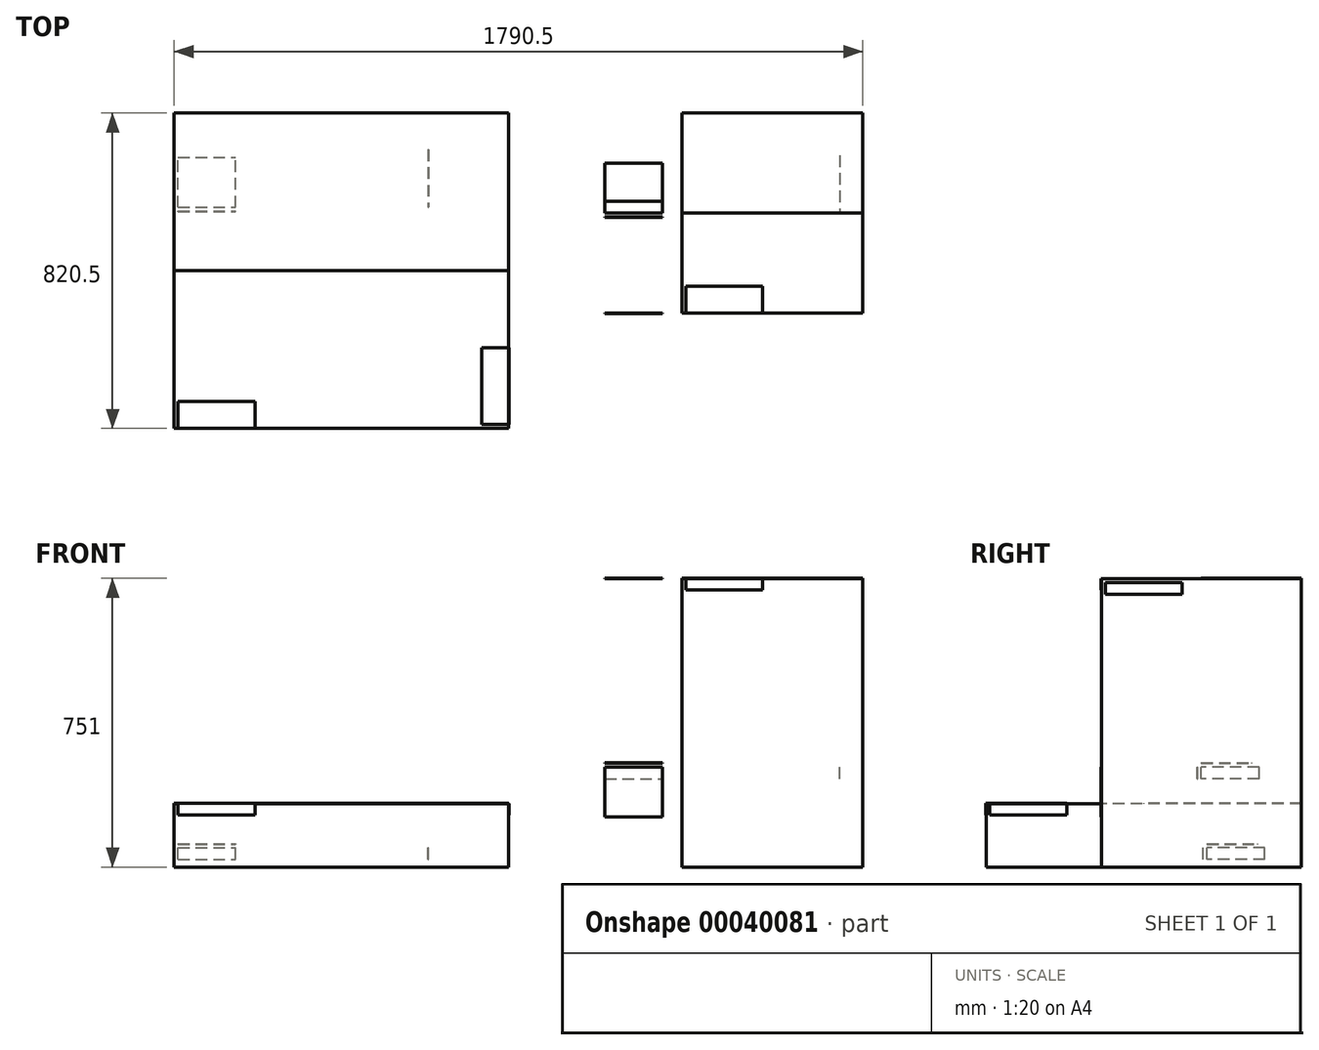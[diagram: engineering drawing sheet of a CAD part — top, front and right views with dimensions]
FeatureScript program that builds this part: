
annotation { "Feature Type Name" : "Feature", "Feature Type Description" : "" }
export const myFeature = defineFeature(function(context is Context, id is Id, definition is map)
    precondition{}
    {
        {
            var Q0;
            Q0=qCreatedBy(makeId("Top.planeOp"),FACE);
            var sketch = newSketch(context, id + "F0", { "sketchPlane" : qUnion([Q0])});
            skLineSegment(sketch, "E0.bottom", {"start": v(-224.33, 780.37) * mm, "end": v(645.67, 780.37) * mm});
            skLineSegment(sketch, "E0.top", {"start": v(-224.33, -39.63) * mm, "end": v(645.67, -39.63) * mm});
            skLineSegment(sketch, "E0.left", {"start": v(-224.33, 780.37) * mm, "end": v(-224.33, -39.63) * mm});
            skLineSegment(sketch, "E0.right", {"start": v(645.67, 780.37) * mm, "end": v(645.67, -39.63) * mm});
            skLineSegment(sketch, "E1.bottom", {"start": v(1095.67, 260.37) * mm, "end": v(1565.67, 260.37) * mm});
            skLineSegment(sketch, "E1.top", {"start": v(1095.67, 780.37) * mm, "end": v(1565.67, 780.37) * mm});
            skLineSegment(sketch, "E1.left", {"start": v(1095.67, 260.37) * mm, "end": v(1095.67, 780.37) * mm});
            skLineSegment(sketch, "E1.right", {"start": v(1565.67, 260.37) * mm, "end": v(1565.67, 780.37) * mm});
            skLineSegment(sketch, "E2.bottom", {"start": v(-224.33, 980.37) * mm, "end": v(-74.33, 980.37) * mm});
            skLineSegment(sketch, "E2.top", {"start": v(-224.33, 1110.37) * mm, "end": v(-74.33, 1110.37) * mm});
            skLineSegment(sketch, "E2.left", {"start": v(-224.33, 980.37) * mm, "end": v(-224.33, 1110.37) * mm});
            skLineSegment(sketch, "E2.right", {"start": v(-74.33, 980.37) * mm, "end": v(-74.33, 1110.37) * mm});
            skLineSegment(sketch, "E3.bottom", {"start": v(-224.33, 880.37) * mm, "end": v(-74.33, 880.37) * mm});
            skLineSegment(sketch, "E3.top", {"start": v(-224.33, 910.37) * mm, "end": v(-74.33, 910.37) * mm});
            skLineSegment(sketch, "E3.left", {"start": v(-224.33, 880.37) * mm, "end": v(-224.33, 910.37) * mm});
            skLineSegment(sketch, "E3.right", {"start": v(-74.33, 880.37) * mm, "end": v(-74.33, 910.37) * mm});
            skSolve(sketch);
        }
        {
            var Q0;
            Q0=makeQuery(id+"F0.imprint","IMPRINT",FACE,{"disambiguationData":[TD([[makeQuery(id+"F0.imprint","IMPRINT",EDGE,{"derivedFrom":sQuery(id+"F0.wireOp",EDGE,"E0.bottom")}),-1.0]])]});
            extrude(context, id + "F1", {"entities" : qUnion([Q0]), "offsetDistance" : 25 * mm, "depth" : 165 * mm});
        }
        {
            var Q0;
            Q0=makeQuery(id+"F0.imprint","IMPRINT",FACE,{"disambiguationData":[TD([[makeQuery(id+"F0.imprint","IMPRINT",EDGE,{"derivedFrom":sQuery(id+"F0.wireOp",EDGE,"E1.bottom")}),1.0]])]});
            extrude(context, id + "F2", {"entities" : qUnion([Q0]), "operationType" : NewBodyOperationType.ADD, "offsetDistance" : 25 * mm, "depth" : 750 * mm});
        }
        {
            var Q0;
            Q0=makeQuery(id+"F0.imprint","IMPRINT",FACE,{"disambiguationData":[TD([[makeQuery(id+"F0.imprint","IMPRINT",EDGE,{"derivedFrom":sQuery(id+"F0.wireOp",EDGE,"E2.bottom")}),1.0]])]});
            var Q1;
            Q1=makeQuery(id+"F0.imprint","IMPRINT",FACE,{"disambiguationData":[TD([[makeQuery(id+"F0.imprint","IMPRINT",EDGE,{"derivedFrom":sQuery(id+"F0.wireOp",EDGE,"E3.bottom")}),1.0]])]});
            extrude(context, id + "F3", {"entities" : qUnion([Q0, Q1]), "depth" : 1 * mm});
        }
        {
            var Q0;
            Q0=makeQuery(id+"F3.opExtrude","SWEPT_BODY",BODY,{"disambiguationData":[OSD([sQuery(id+"F0.wireOp",EDGE,"E2.bottom"),sQuery(id+"F0.wireOp",EDGE,"E2.top"),sQuery(id+"F0.wireOp",EDGE,"E2.left"),sQuery(id+"F0.wireOp",EDGE,"E2.right")])]});
            transform(context, id + "F4", {"entities" : qUnion([Q0]), "transformType" : TransformType.TRANSLATION_3D, "dx" : 10 * mm, "dy" : -445 * mm, "dz" : 60 * mm, "makeCopy" : false});
        }
        {
            var Q0;
            Q0=makeQuery(id+"F3.opExtrude","SWEPT_BODY",BODY,{"disambiguationData":[OSD([sQuery(id+"F0.wireOp",EDGE,"E2.bottom"),sQuery(id+"F0.wireOp",EDGE,"E2.top"),sQuery(id+"F0.wireOp",EDGE,"E2.left"),sQuery(id+"F0.wireOp",EDGE,"E2.right")])]});
            transform(context, id + "F5", {"entities" : qUnion([Q0]), "transformType" : TransformType.TRANSLATION_3D, "dx" : 1110 * mm, "dy" : -15 * mm, "dz" : 210 * mm, "makeCopy" : true});
        }
        {
            var Q0;
            Q0=makeQuery(id+"F3.opExtrude","SWEPT_BODY",BODY,{"disambiguationData":[OSD([sQuery(id+"F0.wireOp",EDGE,"E3.bottom"),sQuery(id+"F0.wireOp",EDGE,"E3.top"),sQuery(id+"F0.wireOp",EDGE,"E3.left"),sQuery(id+"F0.wireOp",EDGE,"E3.right")])]});
            var Q1;
            Q1=makeQuery(id+"F3.opExtrude","CAP_EDGE",EDGE,{"disambiguationData":[OSD([sQuery(id+"F0.wireOp",EDGE,"E3.bottom")])],"isStart":true});
            transform(context, id + "F6", {"entities" : qUnion([Q0]), "transformType" : TransformType.ROTATION, "transformAxis" : qUnion([Q1]), "angle" : 90 * degree, "makeCopy" : false});
        }
        {
            var Q0;
            Q0=makeQuery(id+"F3.opExtrude","SWEPT_BODY",BODY,{"disambiguationData":[OSD([sQuery(id+"F0.wireOp",EDGE,"E3.bottom"),sQuery(id+"F0.wireOp",EDGE,"E3.top"),sQuery(id+"F0.wireOp",EDGE,"E3.left"),sQuery(id+"F0.wireOp",EDGE,"E3.right")])]});
            transform(context, id + "F7", {"entities" : qUnion([Q0]), "transformType" : TransformType.TRANSLATION_3D, "dx" : 10 * mm, "dy" : -355 * mm, "dz" : 20 * mm, "makeCopy" : false});
        }
        {
            var Q0;
            Q0=makeQuery(id+"F3.opExtrude","SWEPT_BODY",BODY,{"disambiguationData":[OSD([sQuery(id+"F0.wireOp",EDGE,"E3.bottom"),sQuery(id+"F0.wireOp",EDGE,"E3.top"),sQuery(id+"F0.wireOp",EDGE,"E3.left"),sQuery(id+"F0.wireOp",EDGE,"E3.right")])]});
            transform(context, id + "F8", {"entities" : qUnion([Q0]), "transformType" : TransformType.TRANSLATION_3D, "dx" : 1110 * mm, "dy" : -15 * mm, "dz" : 210 * mm, "makeCopy" : true});
        }
        {
            var Q0;
            Q0=makeQuery(id+"F3.opExtrude","SWEPT_BODY",BODY,{"disambiguationData":[OSD([sQuery(id+"F0.wireOp",EDGE,"E3.bottom"),sQuery(id+"F0.wireOp",EDGE,"E3.top"),sQuery(id+"F0.wireOp",EDGE,"E3.left"),sQuery(id+"F0.wireOp",EDGE,"E3.right")])]});
            var Q1;
            Q1=makeQuery(id+"F3.opExtrude","CAP_EDGE",EDGE,{"disambiguationData":[OSD([sQuery(id+"F0.wireOp",EDGE,"E3.right")])],"isStart":true});
            transform(context, id + "F9", {"entities" : qUnion([Q0]), "transformType" : TransformType.ROTATION, "transformAxis" : qUnion([Q1]), "angle" : 270 * degree, "makeCopy" : true});
        }
        {
            var Q0;
            Q0=makeQuery(id+"F9.opPattern","COPY",BODY,{"derivedFrom":makeQuery(id+"F3.opExtrude","SWEPT_BODY",BODY,{"disambiguationData":[OSD([sQuery(id+"F0.wireOp",EDGE,"E3.bottom"),sQuery(id+"F0.wireOp",EDGE,"E3.top"),sQuery(id+"F0.wireOp",EDGE,"E3.left"),sQuery(id+"F0.wireOp",EDGE,"E3.right")])]}),"instanceName":"1"});
            transform(context, id + "F10", {"entities" : qUnion([Q0]), "transformType" : TransformType.TRANSLATION_3D, "dx" : 501 * mm, "dy" : 10 * mm, "dz" : 0 * mm, "makeCopy" : false});
        }
        {
            var Q0;
            Q0=makeQuery(id+"F8.opPattern","COPY",BODY,{"derivedFrom":makeQuery(id+"F3.opExtrude","SWEPT_BODY",BODY,{"disambiguationData":[OSD([sQuery(id+"F0.wireOp",EDGE,"E3.bottom"),sQuery(id+"F0.wireOp",EDGE,"E3.top"),sQuery(id+"F0.wireOp",EDGE,"E3.left"),sQuery(id+"F0.wireOp",EDGE,"E3.right")])]}),"instanceName":"1"});
            var Q1;
            Q1=makeQuery(id+"F8.opPattern","COPY",EDGE,{"derivedFrom":makeQuery(id+"F3.opExtrude","CAP_EDGE",EDGE,{"disambiguationData":[OSD([sQuery(id+"F0.wireOp",EDGE,"E3.right")])],"isStart":true}),"instanceName":"1"});
            transform(context, id + "F11", {"entities" : qUnion([Q0]), "transformType" : TransformType.ROTATION, "transformAxis" : qUnion([Q1]), "angle" : 270 * degree, "makeCopy" : true});
        }
        {
            var Q0;
            Q0=makeQuery(id+"F11.opPattern","COPY",BODY,{"derivedFrom":makeQuery(id+"F8.opPattern","COPY",BODY,{"derivedFrom":makeQuery(id+"F3.opExtrude","SWEPT_BODY",BODY,{"disambiguationData":[OSD([sQuery(id+"F0.wireOp",EDGE,"E3.bottom"),sQuery(id+"F0.wireOp",EDGE,"E3.top"),sQuery(id+"F0.wireOp",EDGE,"E3.left"),sQuery(id+"F0.wireOp",EDGE,"E3.right")])]}),"instanceName":"1"}),"instanceName":"1"});
            transform(context, id + "F12", {"entities" : qUnion([Q0]), "transformType" : TransformType.TRANSLATION_3D, "dx" : 461 * mm, "dy" : 10 * mm, "dz" : 0 * mm, "makeCopy" : false});
        }
        {
            var Q0;
            Q0=makeQuery(id+"F2.opExtrude","CAP_FACE",FACE,{"disambiguationData":[OSD([sQuery(id+"F0.wireOp",EDGE,"E1.bottom"),sQuery(id+"F0.wireOp",EDGE,"E1.top"),sQuery(id+"F0.wireOp",EDGE,"E1.left"),sQuery(id+"F0.wireOp",EDGE,"E1.right")])],"isStart":false});
            var sketch = newSketch(context, id + "F13", { "sketchPlane" : qUnion([Q0])});
            skLineSegment(sketch, "E4.bottom", {"start": v(1095.67, 780.37) * mm, "end": v(1565.67, 780.37) * mm});
            skLineSegment(sketch, "E4.top", {"start": v(1095.67, 520.37) * mm, "end": v(1565.67, 520.37) * mm});
            skLineSegment(sketch, "E4.left", {"start": v(1095.67, 780.37) * mm, "end": v(1095.67, 520.37) * mm});
            skLineSegment(sketch, "E4.right", {"start": v(1565.67, 780.37) * mm, "end": v(1565.67, 520.37) * mm});
            skLineSegment(sketch, "E5.bottom", {"start": v(895.67, 520.37) * mm, "end": v(1045.67, 520.37) * mm});
            skLineSegment(sketch, "E5.top", {"start": v(895.67, 550.37) * mm, "end": v(1045.67, 550.37) * mm});
            skLineSegment(sketch, "E5.left", {"start": v(895.67, 520.37) * mm, "end": v(895.67, 550.37) * mm});
            skLineSegment(sketch, "E5.right", {"start": v(1045.67, 520.37) * mm, "end": v(1045.67, 550.37) * mm});
            skSolve(sketch);
        }
        {
            var Q0;
            Q0 = qSketchRegion(id + "F13", true);
            extrude(context, id + "F14", {"entities" : qUnion([Q0]), "depth" : 1 * mm});
        }
        {
            var Q0;
            Q0=makeQuery(id+"F2.opExtrude","SWEPT_FACE",FACE,{"disambiguationData":[OSD([sQuery(id+"F0.wireOp",EDGE,"E1.bottom")])]});
            var sketch = newSketch(context, id + "F15", { "sketchPlane" : qUnion([Q0])});
            skLineSegment(sketch, "E6.bottom", {"start": v(895.67, 260) * mm, "end": v(1045.67, 260) * mm});
            skLineSegment(sketch, "E6.top", {"start": v(895.67, 130) * mm, "end": v(1045.67, 130) * mm});
            skLineSegment(sketch, "E6.left", {"start": v(895.67, 260) * mm, "end": v(895.67, 130) * mm});
            skLineSegment(sketch, "E6.right", {"start": v(1045.67, 260) * mm, "end": v(1045.67, 130) * mm});
            skSolve(sketch);
        }
        {
            var Q0;
            Q0=makeQuery(id+"F15.imprint","IMPRINT",FACE,{"disambiguationData":[TD([[makeQuery(id+"F15.imprint","IMPRINT",EDGE,{"derivedFrom":sQuery(id+"F15.wireOp",EDGE,"E6.bottom")}),-1.0]])]});
            extrude(context, id + "F16", {"entities" : qUnion([Q0]), "depth" : 1 * mm});
        }
        {
            var Q0;
            Q0=makeQuery(id+"F1.opExtrude","CAP_FACE",FACE,{"disambiguationData":[OSD([sQuery(id+"F0.wireOp",EDGE,"E0.bottom"),sQuery(id+"F0.wireOp",EDGE,"E0.top"),sQuery(id+"F0.wireOp",EDGE,"E0.left"),sQuery(id+"F0.wireOp",EDGE,"E0.right")])],"isStart":false});
            var sketch = newSketch(context, id + "F17", { "sketchPlane" : qUnion([Q0])});
            skLineSegment(sketch, "E7.bottom", {"start": v(-214.33, -39.63) * mm, "end": v(-14.33, -39.63) * mm});
            skLineSegment(sketch, "E7.top", {"start": v(-214.33, 30.37) * mm, "end": v(-14.33, 30.37) * mm});
            skLineSegment(sketch, "E7.left", {"start": v(-214.33, -39.63) * mm, "end": v(-214.33, 30.37) * mm});
            skLineSegment(sketch, "E7.right", {"start": v(-14.33, -39.63) * mm, "end": v(-14.33, 30.37) * mm});
            skLineSegment(sketch, "E8.bottom", {"start": v(575.67, 170.37) * mm, "end": v(645.67, 170.37) * mm});
            skLineSegment(sketch, "E8.top", {"start": v(575.67, -29.63) * mm, "end": v(645.67, -29.63) * mm});
            skLineSegment(sketch, "E8.left", {"start": v(575.67, 170.37) * mm, "end": v(575.67, -29.63) * mm});
            skLineSegment(sketch, "E8.right", {"start": v(645.67, 170.37) * mm, "end": v(645.67, -29.63) * mm});
            skSolve(sketch);
        }
        {
            var Q0;
            Q0=makeQuery(id+"F17.imprint","IMPRINT",FACE,{"disambiguationData":[TD([[makeQuery(id+"F17.imprint","IMPRINT",EDGE,{"derivedFrom":sQuery(id+"F17.wireOp",EDGE,"E7.bottom")}),1.0]])]});
            var Q1;
            Q1=makeQuery(id+"F17.imprint","IMPRINT",FACE,{"disambiguationData":[TD([[makeQuery(id+"F17.imprint","IMPRINT",EDGE,{"derivedFrom":sQuery(id+"F17.wireOp",EDGE,"E8.bottom")}),-1.0]])]});
            extrude(context, id + "F18", {"entities" : qUnion([Q0, Q1]), "depth" : 0.5 * mm});
        }
        {
            var Q0;
            Q0=makeQuery(id+"F18.opExtrude","SWEPT_FACE",FACE,{"disambiguationData":[OSD([sQuery(id+"F17.wireOp",EDGE,"E7.bottom")])]});
            var sketch = newSketch(context, id + "F19", { "sketchPlane" : qUnion([Q0])});
            skLineSegment(sketch, "E9.bottom", {"start": v(-214.33, 165.5) * mm, "end": v(-14.33, 165.5) * mm});
            skLineSegment(sketch, "E9.top", {"start": v(-214.33, 135.5) * mm, "end": v(-14.33, 135.5) * mm});
            skLineSegment(sketch, "E9.left", {"start": v(-214.33, 165.5) * mm, "end": v(-214.33, 135.5) * mm});
            skLineSegment(sketch, "E9.right", {"start": v(-14.33, 165.5) * mm, "end": v(-14.33, 135.5) * mm});
            skSolve(sketch);
        }
        {
            var Q0;
            {var subQ0=sQuery(id+"F19.wireOp",EDGE,"E9.top");Q0=makeQuery(id+"F19.imprint","IMPRINT",FACE,{"disambiguationData":[TD([[makeQuery(id+"F19.imprint","IMPRINT",EDGE,{"derivedFrom":subQ0}),1.0]])]});}
            var Q1;
            {var subQ0=sQuery(id+"F19.wireOp",EDGE,"E9.bottom");Q1=makeQuery(id+"F19.imprint","IMPRINT",FACE,{"disambiguationData":[TD([[makeQuery(id+"F19.imprint","IMPRINT",EDGE,{"derivedFrom":subQ0}),-1.0]])]});}
            extrude(context, id + "F20", {"entities" : qUnion([Q0, Q1]), "depth" : 0.5 * mm});
        }
        {
            var Q0;
            Q0=makeQuery(id+"F2.opExtrude","CAP_FACE",FACE,{"disambiguationData":[OSD([sQuery(id+"F0.wireOp",EDGE,"E1.bottom"),sQuery(id+"F0.wireOp",EDGE,"E1.top"),sQuery(id+"F0.wireOp",EDGE,"E1.left"),sQuery(id+"F0.wireOp",EDGE,"E1.right")])],"isStart":false});
            var sketch = newSketch(context, id + "F21", { "sketchPlane" : qUnion([Q0])});
            skLineSegment(sketch, "E10.bottom", {"start": v(1105.67, 260.37) * mm, "end": v(1305.67, 260.37) * mm});
            skLineSegment(sketch, "E10.top", {"start": v(1105.67, 330.37) * mm, "end": v(1305.67, 330.37) * mm});
            skLineSegment(sketch, "E10.left", {"start": v(1105.67, 260.37) * mm, "end": v(1105.67, 330.37) * mm});
            skLineSegment(sketch, "E10.right", {"start": v(1305.67, 260.37) * mm, "end": v(1305.67, 330.37) * mm});
            skSolve(sketch);
        }
        {
            var Q0;
            Q0=makeQuery(id+"F21.imprint","IMPRINT",FACE,{"disambiguationData":[TD([[makeQuery(id+"F21.imprint","IMPRINT",EDGE,{"derivedFrom":sQuery(id+"F21.wireOp",EDGE,"E10.bottom")}),1.0]])]});
            extrude(context, id + "F22", {"entities" : qUnion([Q0]), "depth" : 0.5 * mm});
        }
        {
            var Q0;
            Q0=makeQuery(id+"F22.opExtrude","SWEPT_FACE",FACE,{"disambiguationData":[OSD([sQuery(id+"F21.wireOp",EDGE,"E10.bottom")])]});
            var sketch = newSketch(context, id + "F23", { "sketchPlane" : qUnion([Q0])});
            skLineSegment(sketch, "E11.bottom", {"start": v(1105.67, 750.5) * mm, "end": v(1305.67, 750.5) * mm});
            skLineSegment(sketch, "E11.top", {"start": v(1105.67, 720.5) * mm, "end": v(1305.67, 720.5) * mm});
            skLineSegment(sketch, "E11.left", {"start": v(1105.67, 750.5) * mm, "end": v(1105.67, 720.5) * mm});
            skLineSegment(sketch, "E11.right", {"start": v(1305.67, 750.5) * mm, "end": v(1305.67, 720.5) * mm});
            skSolve(sketch);
        }
        {
            var Q0;
            {var subQ0=sQuery(id+"F23.wireOp",EDGE,"E11.top");Q0=makeQuery(id+"F23.imprint","IMPRINT",FACE,{"disambiguationData":[TD([[makeQuery(id+"F23.imprint","IMPRINT",EDGE,{"derivedFrom":subQ0}),1.0]])]});}
            var Q1;
            {var subQ0=sQuery(id+"F23.wireOp",EDGE,"E11.bottom");Q1=makeQuery(id+"F23.imprint","IMPRINT",FACE,{"disambiguationData":[TD([[makeQuery(id+"F23.imprint","IMPRINT",EDGE,{"derivedFrom":subQ0}),-1.0]])]});}
            extrude(context, id + "F24", {"entities" : qUnion([Q0, Q1]), "depth" : 0.5 * mm});
        }
        {
            var Q0;
            Q0=makeQuery(id+"F1.opExtrude","SWEPT_FACE",FACE,{"disambiguationData":[OSD([sQuery(id+"F0.wireOp",EDGE,"E0.right")])]});
            var sketch = newSketch(context, id + "F25", { "sketchPlane" : qUnion([Q0])});
            skLineSegment(sketch, "E12.bottom", {"start": v(-29.63, 165) * mm, "end": v(170.37, 165) * mm});
            skLineSegment(sketch, "E12.top", {"start": v(-29.63, 135) * mm, "end": v(170.37, 135) * mm});
            skLineSegment(sketch, "E12.left", {"start": v(-29.63, 165) * mm, "end": v(-29.63, 135) * mm});
            skLineSegment(sketch, "E12.right", {"start": v(170.37, 165) * mm, "end": v(170.37, 135) * mm});
            skSolve(sketch);
        }
        {
            var Q0;
            Q0=makeQuery(id+"F25.imprint","IMPRINT",FACE,{"disambiguationData":[TD([[makeQuery(id+"F25.imprint","IMPRINT",EDGE,{"derivedFrom":sQuery(id+"F25.wireOp",EDGE,"E12.bottom")}),1.0]])]});
            extrude(context, id + "F26", {"entities" : qUnion([Q0]), "depth" : 0.5 * mm});
        }
        {
            var Q0;
            Q0=makeQuery(id+"F2.opExtrude","SWEPT_FACE",FACE,{"disambiguationData":[OSD([sQuery(id+"F0.wireOp",EDGE,"E1.right")])]});
            var sketch = newSketch(context, id + "F27", { "sketchPlane" : qUnion([Q0])});
            skLineSegment(sketch, "E13.bottom", {"start": v(270.37, 740) * mm, "end": v(470.37, 740) * mm});
            skLineSegment(sketch, "E13.top", {"start": v(270.37, 710) * mm, "end": v(470.37, 710) * mm});
            skLineSegment(sketch, "E13.left", {"start": v(270.37, 740) * mm, "end": v(270.37, 710) * mm});
            skLineSegment(sketch, "E13.right", {"start": v(470.37, 740) * mm, "end": v(470.37, 710) * mm});
            skSolve(sketch);
        }
        {
            var Q0;
            Q0=makeQuery(id+"F27.imprint","IMPRINT",FACE,{"disambiguationData":[TD([[makeQuery(id+"F27.imprint","IMPRINT",EDGE,{"derivedFrom":sQuery(id+"F27.wireOp",EDGE,"E13.bottom")}),-1.0]])]});
            extrude(context, id + "F28", {"entities" : qUnion([Q0]), "depth" : 0.5 * mm});
        }
        {
            var Q0;
            Q0=makeQuery(id+"F1.opExtrude","CAP_FACE",FACE,{"disambiguationData":[OSD([sQuery(id+"F0.wireOp",EDGE,"E0.bottom"),sQuery(id+"F0.wireOp",EDGE,"E0.top"),sQuery(id+"F0.wireOp",EDGE,"E0.left"),sQuery(id+"F0.wireOp",EDGE,"E0.right")])],"isStart":false});
            var sketch = newSketch(context, id + "F29", { "sketchPlane" : qUnion([Q0])});
            skLineSegment(sketch, "E14.bottom", {"start": v(-224.33, 780.37) * mm, "end": v(645.67, 780.37) * mm});
            skLineSegment(sketch, "E14.top", {"start": v(-224.33, 370.37) * mm, "end": v(645.67, 370.37) * mm});
            skLineSegment(sketch, "E14.left", {"start": v(-224.33, 780.37) * mm, "end": v(-224.33, 370.37) * mm});
            skLineSegment(sketch, "E14.right", {"start": v(645.67, 780.37) * mm, "end": v(645.67, 370.37) * mm});
            skSolve(sketch);
        }
        {
            var Q0;
            Q0 = qSketchRegion(id + "F29", true);
            extrude(context, id + "F30", {"entities" : qUnion([Q0]), "depth" : 1 * mm, "offsetDistance" : 25 * mm});
        }
    });
